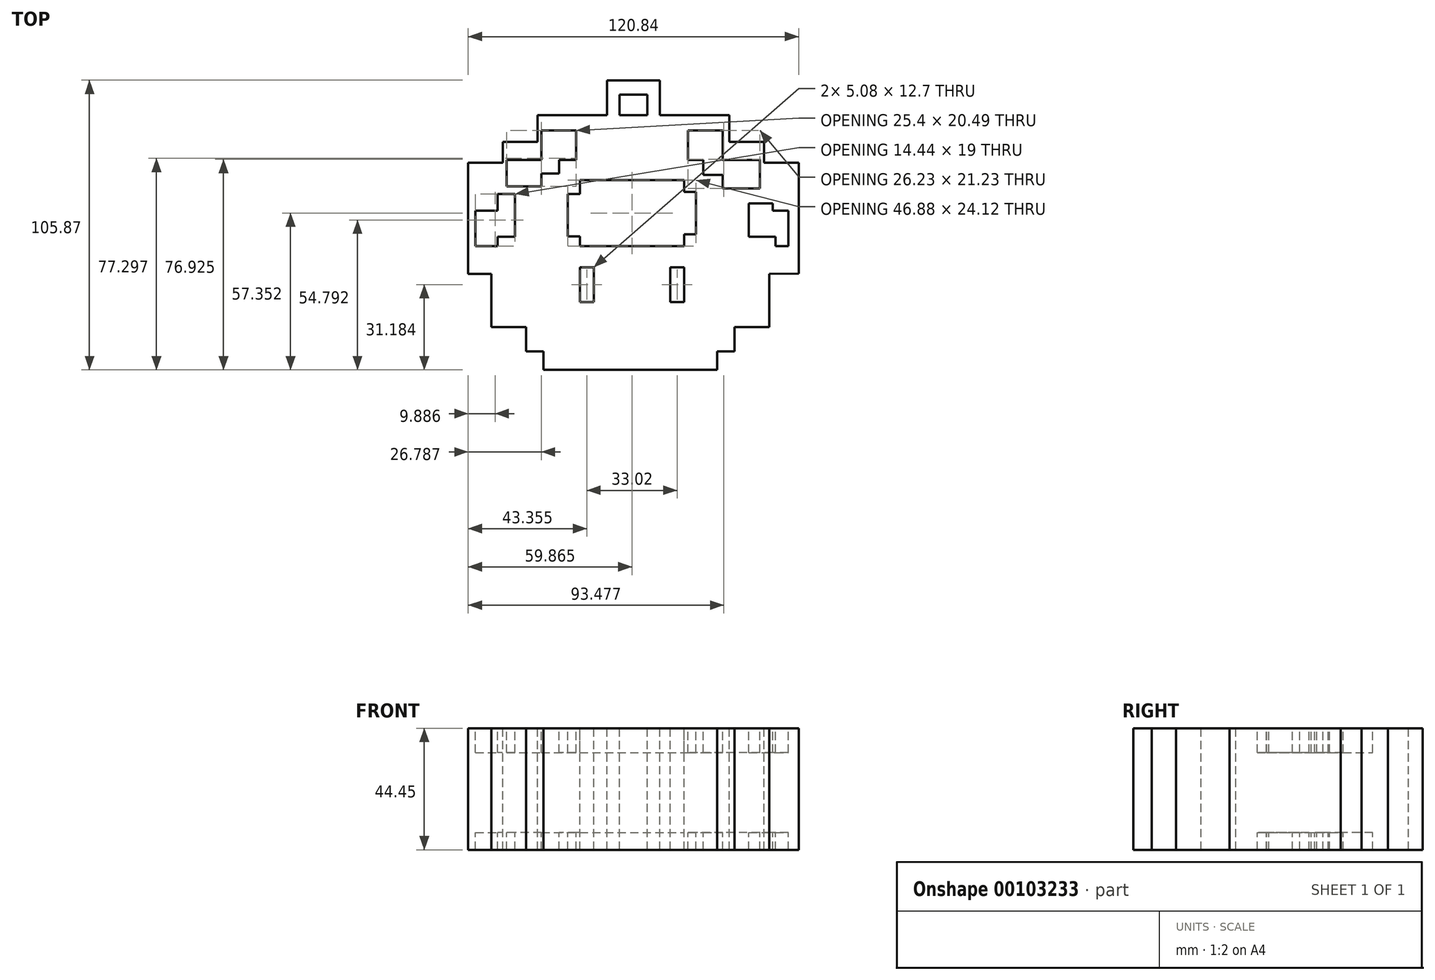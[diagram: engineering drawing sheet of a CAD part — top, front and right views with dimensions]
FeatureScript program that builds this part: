
annotation { "Feature Type Name" : "Feature", "Feature Type Description" : "" }
export const myFeature = defineFeature(function(context is Context, id is Id, definition is map)
    precondition{}
    {
        {
            var Q0;
            Q0=qCreatedBy(makeId("Top.planeOp"),FACE);
            var sketch = newSketch(context, id + "F0", { "sketchPlane" : qUnion([Q0])});
            skLineSegment(sketch, "E0", {"start": v(62.48, 21.67) * mm, "end": v(62.48, 21.67) * mm});
            skLineSegment(sketch, "E1", {"start": v(-64.52, 21.67) * mm, "end": v(-64.52, 21.67) * mm});
            skLineSegment(sketch, "E2", {"start": v(59.93, 30.48) * mm, "end": v(47.23, 30.48) * mm});
            skLineSegment(sketch, "E3", {"start": v(-60.9, 30.48) * mm, "end": v(-48.2, 30.48) * mm});
            skLineSegment(sketch, "E4", {"start": v(-48.2, 30.48) * mm, "end": v(-48.2, 38.1) * mm});
            skLineSegment(sketch, "E5", {"start": v(47.23, 30.48) * mm, "end": v(47.23, 38.1) * mm});
            skLineSegment(sketch, "E6", {"start": v(47.23, 38.1) * mm, "end": v(34.53, 38.1) * mm});
            skLineSegment(sketch, "E7", {"start": v(-48.2, 38.1) * mm, "end": v(-35.5, 38.1) * mm});
            skLineSegment(sketch, "E8", {"start": v(-35.5, 38.1) * mm, "end": v(-35.5, 47.88) * mm});
            skLineSegment(sketch, "E9", {"start": v(34.53, 47.88) * mm, "end": v(34.53, 38.1) * mm});
            skLineSegment(sketch, "E10", {"start": v(-60.9, 30.48) * mm, "end": v(-60.9, -10.16) * mm});
            skLineSegment(sketch, "E11", {"start": v(-52.46, -10.16) * mm, "end": v(-52.46, -29.64) * mm});
            skLineSegment(sketch, "E12", {"start": v(-52.46, -29.64) * mm, "end": v(-39.76, -29.64) * mm});
            skLineSegment(sketch, "E13", {"start": v(49.14, -10.16) * mm, "end": v(49.14, -29.64) * mm});
            skLineSegment(sketch, "E14", {"start": v(49.14, -29.64) * mm, "end": v(36.44, -29.64) * mm});
            skLineSegment(sketch, "E15", {"start": v(36.44, -29.64) * mm, "end": v(36.44, -38.58) * mm});
            skLineSegment(sketch, "E16", {"start": v(-39.76, -29.64) * mm, "end": v(-39.76, -38.58) * mm});
            skLineSegment(sketch, "E17", {"start": v(-39.76, -38.58) * mm, "end": v(-33.4, -38.58) * mm});
            skLineSegment(sketch, "E18", {"start": v(36.44, -38.58) * mm, "end": v(30.1, -38.58) * mm});
            skLineSegment(sketch, "E19", {"start": v(30.1, -38.58) * mm, "end": v(30.1, -45.29) * mm});
            skLineSegment(sketch, "E20", {"start": v(30.1, -45.29) * mm, "end": v(-33.4, -45.29) * mm});
            skLineSegment(sketch, "E21", {"start": v(-33.4, -45.29) * mm, "end": v(-33.4, -38.58) * mm});
            skLineSegment(sketch, "E22", {"start": v(-58.25, 21.76) * mm, "end": v(-58.25, -8.02) * mm});
            skLineSegment(sketch, "E23", {"start": v(-58.25, -8.02) * mm, "end": v(-40.42, -8.02) * mm});
            skPoint(sketch, "E24.endSnap0", {"position": v(35.62, -7.3) * mm});
            skLineSegment(sketch, "E25", {"start": v(38.32, -7.3) * mm, "end": v(56.16, -7.3) * mm});
            skLineSegment(sketch, "E26", {"start": v(56.16, -7.3) * mm, "end": v(56.16, 21.02) * mm});
            skLineSegment(sketch, "E27", {"start": v(56.16, 21.02) * mm, "end": v(45.68, 21.02) * mm});
            skLineSegment(sketch, "E28", {"start": v(45.68, 21.02) * mm, "end": v(45.68, 31.45) * mm});
            skLineSegment(sketch, "E29", {"start": v(45.68, 31.45) * mm, "end": v(32.15, 31.45) * mm});
            skLineSegment(sketch, "E30", {"start": v(32.15, 31.45) * mm, "end": v(32.15, 42.25) * mm});
            skLineSegment(sketch, "E31", {"start": v(-34.12, 42.25) * mm, "end": v(-34.12, 31.45) * mm});
            skLineSegment(sketch, "E32", {"start": v(-34.12, 31.45) * mm, "end": v(-46.82, 31.45) * mm});
            skLineSegment(sketch, "E33", {"start": v(-46.82, 31.45) * mm, "end": v(-46.82, 21.76) * mm});
            skLineSegment(sketch, "E34", {"start": v(-46.82, 21.76) * mm, "end": v(-58.25, 21.76) * mm});
            skLineSegment(sketch, "E35", {"start": v(44.25, -16.65) * mm, "end": v(44.25, -26.29) * mm});
            skLineSegment(sketch, "E36", {"start": v(44.25, -26.29) * mm, "end": v(31.55, -26.29) * mm});
            skLineSegment(sketch, "E37", {"start": v(31.55, -26.29) * mm, "end": v(31.55, -32.25) * mm});
            skLineSegment(sketch, "E38", {"start": v(31.55, -32.25) * mm, "end": v(25.2, -32.25) * mm});
            skLineSegment(sketch, "E39", {"start": v(25.2, -32.25) * mm, "end": v(25.2, -41.19) * mm});
            skLineSegment(sketch, "E40", {"start": v(25.2, -41.19) * mm, "end": v(-28.4, -41.19) * mm});
            skLineSegment(sketch, "E41", {"start": v(-28.4, -41.19) * mm, "end": v(-28.4, -34.48) * mm});
            skLineSegment(sketch, "E42", {"start": v(-28.4, -34.48) * mm, "end": v(-34.74, -34.48) * mm});
            skLineSegment(sketch, "E43", {"start": v(-34.74, -34.48) * mm, "end": v(-34.74, -26.29) * mm});
            skLineSegment(sketch, "E44", {"start": v(-34.74, -26.29) * mm, "end": v(-47.44, -26.29) * mm});
            skLineSegment(sketch, "E45", {"start": v(-47.44, -26.29) * mm, "end": v(-47.44, -16.65) * mm});
            skLineSegment(sketch, "E46", {"start": v(-47.44, -16.65) * mm, "end": v(-34.74, -16.65) * mm});
            skLineSegment(sketch, "E47", {"start": v(-34.74, -16.65) * mm, "end": v(-34.74, -7.76) * mm});
            skLineSegment(sketch, "E48", {"start": v(-34.74, -7.76) * mm, "end": v(31.55, -7.76) * mm});
            skLineSegment(sketch, "E49", {"start": v(31.55, -7.76) * mm, "end": v(31.55, -16.65) * mm});
            skLineSegment(sketch, "E50", {"start": v(31.55, -16.65) * mm, "end": v(44.25, -16.65) * mm});
            skLineSegment(sketch, "E51", {"start": v(-21.42, 42.25) * mm, "end": v(-21.42, 31.45) * mm});
            skLineSegment(sketch, "E52", {"start": v(-34.12, 42.25) * mm, "end": v(-21.42, 42.25) * mm});
            skLineSegment(sketch, "E53", {"start": v(-46.82, 21.76) * mm, "end": v(-34.12, 21.76) * mm});
            skLineSegment(sketch, "E54", {"start": v(-34.12, 21.76) * mm, "end": v(-34.12, 26.48) * mm});
            skLineSegment(sketch, "E55", {"start": v(-34.12, 26.48) * mm, "end": v(-27.7, 26.48) * mm});
            skLineSegment(sketch, "E56", {"start": v(-27.7, 26.48) * mm, "end": v(-27.7, 31.45) * mm});
            skLineSegment(sketch, "E57", {"start": v(-21.42, 31.45) * mm, "end": v(-27.7, 31.45) * mm});
            skLineSegment(sketch, "E58", {"start": v(32.15, 42.25) * mm, "end": v(19.45, 42.25) * mm});
            skLineSegment(sketch, "E59", {"start": v(19.45, 42.25) * mm, "end": v(19.45, 31.45) * mm});
            skLineSegment(sketch, "E60", {"start": v(19.45, 31.45) * mm, "end": v(25.05, 31.45) * mm});
            skLineSegment(sketch, "E61", {"start": v(25.05, 31.45) * mm, "end": v(25.05, 25.95) * mm});
            skLineSegment(sketch, "E62", {"start": v(25.05, 25.95) * mm, "end": v(32.15, 25.95) * mm});
            skLineSegment(sketch, "E63", {"start": v(45.68, 21.02) * mm, "end": v(32.15, 21.02) * mm});
            skLineSegment(sketch, "E64", {"start": v(32.15, 21.02) * mm, "end": v(32.15, 25.95) * mm});
            skLineSegment(sketch, "E65", {"start": v(-21.42, 42.25) * mm, "end": v(19.45, 42.25) * mm});
            skLineSegment(sketch, "E66", {"start": v(-58.25, 12.95) * mm, "end": v(-50.09, 12.95) * mm});
            skLineSegment(sketch, "E67", {"start": v(-50.09, 12.95) * mm, "end": v(-50.09, 19) * mm});
            skLineSegment(sketch, "E68", {"start": v(-50.09, 19) * mm, "end": v(-43.8, 19) * mm});
            skLineSegment(sketch, "E69", {"start": v(-43.8, 19) * mm, "end": v(-43.8, 3.4) * mm});
            skLineSegment(sketch, "E70", {"start": v(-43.8, 3.4) * mm, "end": v(-50.09, 3.4) * mm});
            skLineSegment(sketch, "E71", {"start": v(-50.09, 3.4) * mm, "end": v(-50.09, 0) * mm});
            skLineSegment(sketch, "E72", {"start": v(-50.09, 0) * mm, "end": v(-58.25, 0) * mm});
            skLineSegment(sketch, "E73", {"start": v(56.16, 12.95) * mm, "end": v(50.46, 12.95) * mm});
            skLineSegment(sketch, "E74", {"start": v(50.46, 12.95) * mm, "end": v(50.46, 15.51) * mm});
            skLineSegment(sketch, "E75", {"start": v(50.46, 15.51) * mm, "end": v(41.71, 15.51) * mm});
            skLineSegment(sketch, "E76", {"start": v(41.71, 15.51) * mm, "end": v(41.71, 3.4) * mm});
            skLineSegment(sketch, "E77", {"start": v(41.71, 3.4) * mm, "end": v(51.4, 3.4) * mm});
            skLineSegment(sketch, "E78", {"start": v(51.4, 3.4) * mm, "end": v(51.4, 0) * mm});
            skLineSegment(sketch, "E79", {"start": v(51.4, 0) * mm, "end": v(56.16, 0) * mm});
            skLineSegment(sketch, "E80", {"start": v(-20.1, 0) * mm, "end": v(18, 0) * mm});
            skLineSegment(sketch, "E81", {"start": v(18, 0) * mm, "end": v(18, 4.2) * mm});
            skLineSegment(sketch, "E82", {"start": v(-20.1, 0) * mm, "end": v(-20.1, 3.51) * mm});
            skLineSegment(sketch, "E83", {"start": v(-20.1, 3.51) * mm, "end": v(-24.48, 3.51) * mm});
            skLineSegment(sketch, "E84", {"start": v(-24.48, 3.51) * mm, "end": v(-24.48, 19) * mm});
            skLineSegment(sketch, "E85", {"start": v(-24.48, 19) * mm, "end": v(-20.1, 19) * mm});
            skLineSegment(sketch, "E86", {"start": v(-20.1, 19) * mm, "end": v(-20.1, 24.12) * mm});
            skLineSegment(sketch, "E87", {"start": v(18, 4.2) * mm, "end": v(22.4, 4.2) * mm});
            skLineSegment(sketch, "E88", {"start": v(22.4, 4.2) * mm, "end": v(22.4, 19.7) * mm});
            skLineSegment(sketch, "E89", {"start": v(22.4, 19.7) * mm, "end": v(18, 19.7) * mm});
            skLineSegment(sketch, "E90", {"start": v(-20.1, 24.12) * mm, "end": v(18, 24.12) * mm});
            skLineSegment(sketch, "E91", {"start": v(18, 24.12) * mm, "end": v(18, 19.7) * mm});
            skLineSegment(sketch, "E92", {"start": v(38.32, -7.3) * mm, "end": v(38.32, 0) * mm});
            skLineSegment(sketch, "E93", {"start": v(38.32, 0) * mm, "end": v(-40.42, 0) * mm});
            skLineSegment(sketch, "E94", {"start": v(-40.42, 0) * mm, "end": v(-40.42, -8.02) * mm});
            skLineSegment(sketch, "E95", {"start": v(-60.9, -10.16) * mm, "end": v(-52.46, -10.16) * mm});
            skLineSegment(sketch, "E96", {"start": v(49.14, -10.16) * mm, "end": v(33.9, -10.16) * mm});
            skLineSegment(sketch, "E97", {"start": v(33.9, -10.16) * mm, "end": v(33.9, -4.81) * mm});
            skLineSegment(sketch, "E98", {"start": v(33.9, -4.81) * mm, "end": v(-37.22, -4.81) * mm});
            skLineSegment(sketch, "E99", {"start": v(-37.22, -4.81) * mm, "end": v(-37.22, -10.16) * mm});
            skLineSegment(sketch, "E100", {"start": v(-37.22, -10.16) * mm, "end": v(-52.46, -10.16) * mm});
            skLineSegment(sketch, "E101", {"start": v(-35.5, 47.88) * mm, "end": v(-10.1, 47.88) * mm});
            skLineSegment(sketch, "E102", {"start": v(34.53, 47.88) * mm, "end": v(9.13, 47.88) * mm});
            skLineSegment(sketch, "E103", {"start": v(-10.1, 47.88) * mm, "end": v(-10.1, 60.58) * mm});
            skLineSegment(sketch, "E104", {"start": v(-10.1, 60.58) * mm, "end": v(9.13, 60.58) * mm});
            skLineSegment(sketch, "E105", {"start": v(9.13, 60.58) * mm, "end": v(9.13, 47.88) * mm});
            skLineSegment(sketch, "E106", {"start": v(-5.57, 47.88) * mm, "end": v(-5.57, 55.28) * mm});
            skLineSegment(sketch, "E107", {"start": v(-5.57, 55.28) * mm, "end": v(4.6, 55.28) * mm});
            skLineSegment(sketch, "E108", {"start": v(4.6, 55.28) * mm, "end": v(4.6, 47.88) * mm});
            skLineSegment(sketch, "E109", {"start": v(4.6, 47.88) * mm, "end": v(9.13, 47.88) * mm});
            skLineSegment(sketch, "E110", {"start": v(-10.1, 47.88) * mm, "end": v(-5.57, 47.88) * mm});
            skLineSegment(sketch, "E111", {"start": v(-5.57, 47.88) * mm, "end": v(4.6, 47.88) * mm});
            skLineSegment(sketch, "E112", {"start": v(-20.1, -7.76) * mm, "end": v(-20.1, -20.46) * mm});
            skLineSegment(sketch, "E113", {"start": v(-20.1, -20.46) * mm, "end": v(-15.02, -20.46) * mm});
            skLineSegment(sketch, "E114", {"start": v(-15.02, -20.46) * mm, "end": v(-15.02, -7.76) * mm});
            skLineSegment(sketch, "E115", {"start": v(-15.02, -7.76) * mm, "end": v(-20.1, -7.76) * mm});
            skLineSegment(sketch, "E116", {"start": v(18, -7.76) * mm, "end": v(18, -20.46) * mm});
            skLineSegment(sketch, "E117", {"start": v(18, -20.46) * mm, "end": v(12.92, -20.46) * mm});
            skLineSegment(sketch, "E118", {"start": v(12.92, -20.46) * mm, "end": v(12.92, -7.76) * mm});
            skLineSegment(sketch, "E119", {"start": v(12.92, -7.76) * mm, "end": v(18, -7.76) * mm});
            skLineSegment(sketch, "E120", {"start": v(59.93, 30.48) * mm, "end": v(59.93, -10.08) * mm});
            skPoint(sketch, "E121.start.orphan", {"position": v(61.84, -10.08) * mm});
            skLineSegment(sketch, "E122", {"start": v(59.93, -10.08) * mm, "end": v(49.14, -10.16) * mm});
            skSolve(sketch);
        }
        {
            var Q0;
            {var subQ9=sQuery(id+"F0.wireOp",EDGE,"E23");Q0=makeQuery(id+"F0.imprint","IMPRINT",FACE,{"disambiguationData":[TD([[makeQuery(id+"F0.imprint","IMPRINT",EDGE,{"derivedFrom":subQ9}),1.0]])]});}
            var Q1;
            Q1=makeQuery(id+"F0.imprint","IMPRINT",FACE,{"disambiguationData":[TD([[makeQuery(id+"F0.imprint","IMPRINT",EDGE,{"derivedFrom":sQuery(id+"F0.wireOp",EDGE,"E2")}),1.0]])]});
            var Q2;
            Q2=makeQuery(id+"F0.imprint","IMPRINT",FACE,{"disambiguationData":[TD([[makeQuery(id+"F0.imprint","IMPRINT",EDGE,{"derivedFrom":sQuery(id+"F0.wireOp",EDGE,"E103")}),-1.0]])]});
            var Q3;
            Q3=makeQuery(id+"F0.imprint","IMPRINT",FACE,{"disambiguationData":[TD([[makeQuery(id+"F0.imprint","IMPRINT",EDGE,{"derivedFrom":sQuery(id+"F0.wireOp",EDGE,"E35")}),-1.0]])]});
            var Q4;
            Q4=makeQuery(id+"F0.imprint","IMPRINT",FACE,{"disambiguationData":[TD([[makeQuery(id+"F0.imprint","IMPRINT",EDGE,{"derivedFrom":sQuery(id+"F0.wireOp",EDGE,"E11")}),1.0]])]});
            extrude(context, id + "F1", {"entities" : qUnion([Q0, Q1, Q2, Q3, Q4]), "oppositeDirection" : true, "depth" : 44.45 * mm});
        }
        {
            var Q0;
            Q0=makeQuery(id+"F0.imprint","IMPRINT",FACE,{"disambiguationData":[TD([[makeQuery(id+"F0.imprint","IMPRINT",EDGE,{"derivedFrom":sQuery(id+"F0.wireOp",EDGE,"E28")}),1.0]])]});
            var Q1;
            {var subQ0=sQuery(id+"F0.wireOp",EDGE,"E73");Q1=makeQuery(id+"F0.imprint","IMPRINT",FACE,{"disambiguationData":[TD([[makeQuery(id+"F0.imprint","IMPRINT",EDGE,{"derivedFrom":subQ0}),1.0]])]});}
            var Q2;
            Q2=makeQuery(id+"F0.imprint","IMPRINT",FACE,{"disambiguationData":[TD([[makeQuery(id+"F0.imprint","IMPRINT",EDGE,{"derivedFrom":sQuery(id+"F0.wireOp",EDGE,"E80")}),1.0]])]});
            var Q3;
            Q3=makeQuery(id+"F0.imprint","IMPRINT",FACE,{"disambiguationData":[TD([[makeQuery(id+"F0.imprint","IMPRINT",EDGE,{"derivedFrom":sQuery(id+"F0.wireOp",EDGE,"E31")}),1.0]])]});
            var Q4;
            {var subQ0=sQuery(id+"F0.wireOp",EDGE,"E66");Q4=makeQuery(id+"F0.imprint","IMPRINT",FACE,{"disambiguationData":[TD([[makeQuery(id+"F0.imprint","IMPRINT",EDGE,{"derivedFrom":subQ0}),-1.0]])]});}
            extrude(context, id + "F2", {"entities" : qUnion([Q0, Q1, Q2, Q3, Q4]), "operationType" : NewBodyOperationType.ADD, "oppositeDirection" : true, "depth" : 38.1 * mm});
        }
        {
            var Q0;
            {var subQ0=sQuery(id+"F0.wireOp",EDGE,"E66");Q0=makeQuery(id+"F0.imprint","IMPRINT",FACE,{"disambiguationData":[TD([[makeQuery(id+"F0.imprint","IMPRINT",EDGE,{"derivedFrom":subQ0}),-1.0]])]});}
            var Q1;
            Q1=makeQuery(id+"F0.imprint","IMPRINT",FACE,{"disambiguationData":[TD([[makeQuery(id+"F0.imprint","IMPRINT",EDGE,{"derivedFrom":sQuery(id+"F0.wireOp",EDGE,"E31")}),1.0]])]});
            var Q2;
            Q2=makeQuery(id+"F0.imprint","IMPRINT",FACE,{"disambiguationData":[TD([[makeQuery(id+"F0.imprint","IMPRINT",EDGE,{"derivedFrom":sQuery(id+"F0.wireOp",EDGE,"E80")}),1.0]])]});
            var Q3;
            Q3=makeQuery(id+"F0.imprint","IMPRINT",FACE,{"disambiguationData":[TD([[makeQuery(id+"F0.imprint","IMPRINT",EDGE,{"derivedFrom":sQuery(id+"F0.wireOp",EDGE,"E28")}),1.0]])]});
            var Q4;
            {var subQ0=sQuery(id+"F0.wireOp",EDGE,"E73");Q4=makeQuery(id+"F0.imprint","IMPRINT",FACE,{"disambiguationData":[TD([[makeQuery(id+"F0.imprint","IMPRINT",EDGE,{"derivedFrom":subQ0}),1.0]])]});}
            extrude(context, id + "F3", {"entities" : qUnion([Q0, Q1, Q2, Q3, Q4]), "operationType" : NewBodyOperationType.REMOVE, "oppositeDirection" : true, "depth" : 8.93 * mm});
        }
    });
